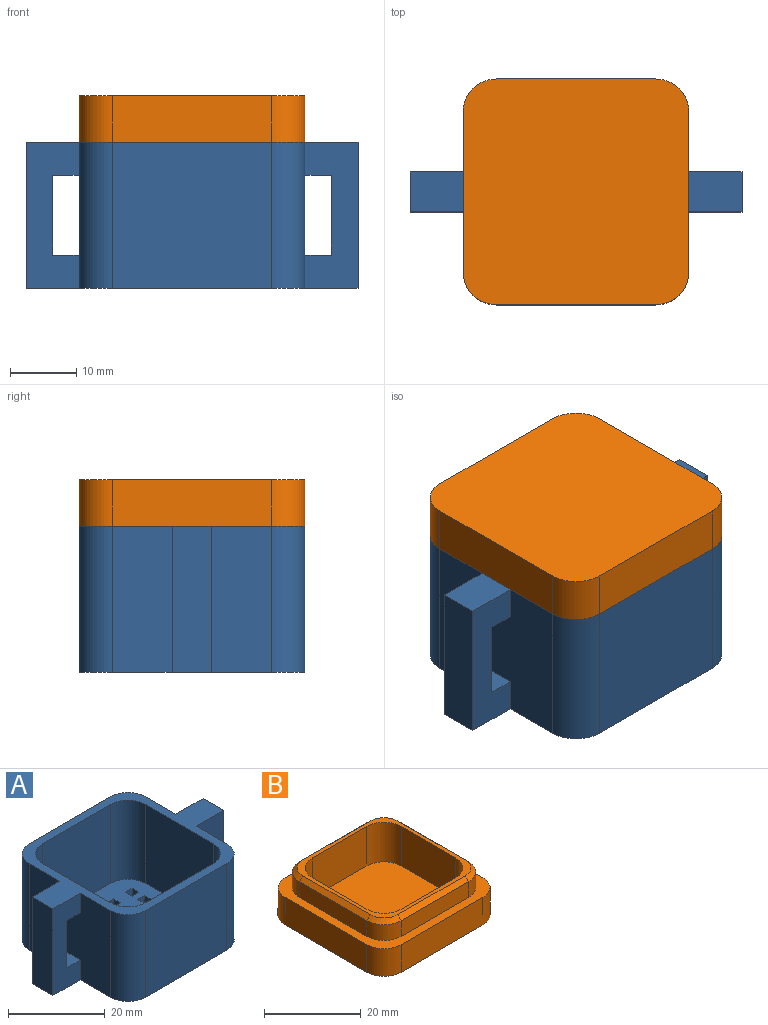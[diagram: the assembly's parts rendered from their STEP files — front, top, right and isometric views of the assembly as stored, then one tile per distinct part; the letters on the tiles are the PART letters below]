
ASSEMBLY  parts=2 mates=1
PART A: 77 faces, bbox 50x34x22 mm
  f0: plane 24x22mm, normal (-1,0,0), area 468mm2, adj f2,f10,f57,f58,f71,f72,f73,f76
  f1: plane 30x30mm, normal (0,0,1), area 738mm2, adj f5,f6,f7,f8,f11,f12,f13,f14
  f2: plane 50x34mm, normal (0,0,-1), area 1124.2mm2, adj f0,f3,f4,f9,f11,f12,f13,f14
  f3: plane 24x22mm, normal (0,1,0), area 528mm2, adj f2,f10,f57,f60
  f4: plane 24x22mm, normal (0,-1,0), area 528mm2, adj f2,f10,f58,f59
  f5: plane 20x20mm, normal (1,0,0), area 400mm2, adj f1,f10,f61,f64
  f6: plane 20x20mm, normal (0,-1,0), area 400mm2, adj f1,f10,f61,f62
  f7: plane 20x20mm, normal (-1,0,0), area 400mm2, adj f1,f10,f62,f63
  f8: plane 20x20mm, normal (0,1,0), area 400mm2, adj f1,f10,f63,f64
  f9: plane 24x22mm, normal (1,0,0), area 468mm2, adj f2,f10,f59,f60,f65,f66,f67,f70
  f10: plane 50x34mm, normal (0,0,1), area 352mm2, adj f0,f3,f4,f5,f6,f7,f8,f9
  f11: plane 2x2mm, normal (1,0,0), area 4mm2, adj f1,f2,f12,f14
  f12: plane 2x2mm, normal (0,-1,0), area 4mm2, adj f1,f2,f11,f13
  f13: plane 2x2mm, normal (-1,0,0), area 4mm2, adj f1,f2,f12,f14
  f14: plane 2x2mm, normal (0,1,0), area 4mm2, adj f1,f2,f11,f13
  f15: plane 2x2mm, normal (-1,0,0), area 4mm2, adj f1,f2,f16,f18
  f16: plane 2x2mm, normal (0,1,0), area 4mm2, adj f1,f2,f15,f17
  f17: plane 2x2mm, normal (1,0,0), area 4mm2, adj f1,f2,f16,f18
  f18: plane 2x2mm, normal (0,-1,0), area 4mm2, adj f1,f2,f15,f17
  f19: plane 2x2mm, normal (-1,0,0), area 4mm2, adj f1,f2,f20,f22
  f20: plane 2x2mm, normal (0,1,0), area 4mm2, adj f1,f2,f19,f21
  f21: plane 2x2mm, normal (1,0,0), area 4mm2, adj f1,f2,f20,f22
  f22: plane 2x2mm, normal (0,-1,0), area 4mm2, adj f1,f2,f19,f21
  f23: plane 2x2mm, normal (-1,0,0), area 4mm2, adj f1,f2,f24,f26
  f24: plane 2x2mm, normal (0,1,0), area 4mm2, adj f1,f2,f23,f25
  f25: plane 2x2mm, normal (1,0,0), area 4mm2, adj f1,f2,f24,f26
  f26: plane 2x2mm, normal (0,-1,0), area 4mm2, adj f1,f2,f23,f25
  f27: plane 2x2mm, normal (-1,0,0), area 4mm2, adj f1,f2,f28,f30
  f28: plane 2x2mm, normal (0,1,0), area 4mm2, adj f1,f2,f27,f29
  f29: plane 2x2mm, normal (1,0,0), area 4mm2, adj f1,f2,f28,f30
  f30: plane 2x2mm, normal (0,-1,0), area 4mm2, adj f1,f2,f27,f29
  f31: plane 2x2mm, normal (-1,0,0), area 4mm2, adj f1,f2,f32,f34
  f32: plane 2x2mm, normal (0,1,0), area 4mm2, adj f1,f2,f31,f33
  f33: plane 2x2mm, normal (1,0,0), area 4mm2, adj f1,f2,f32,f34
  f34: plane 2x2mm, normal (0,-1,0), area 4mm2, adj f1,f2,f31,f33
  f35: plane 2x2mm, normal (-1,0,0), area 4mm2, adj f1,f2,f36,f38
  f36: plane 2x2mm, normal (0,1,0), area 4mm2, adj f1,f2,f35,f37
  f37: plane 2x2mm, normal (1,0,0), area 4mm2, adj f1,f2,f36,f38
  f38: plane 2x2mm, normal (0,-1,0), area 4mm2, adj f1,f2,f35,f37
  f39: plane 2x2mm, normal (-1,0,0), area 4mm2, adj f1,f2,f40,f42
  f40: plane 2x2mm, normal (0,1,0), area 4mm2, adj f1,f2,f39,f41
  f41: plane 2x2mm, normal (1,0,0), area 4mm2, adj f1,f2,f40,f42
  f42: plane 2x2mm, normal (0,-1,0), area 4mm2, adj f1,f2,f39,f41
  f43: plane 2x2mm, normal (-1,0,0), area 4mm2, adj f1,f2,f44,f46
  f44: plane 2x2mm, normal (0,1,0), area 4mm2, adj f1,f2,f43,f45
  f45: plane 2x2mm, normal (1,0,0), area 4mm2, adj f1,f2,f44,f46
  f46: plane 2x2mm, normal (0,-1,0), area 4mm2, adj f1,f2,f43,f45
  f47: plane 2x2mm, normal (-1,0,0), area 4mm2, adj f1,f2,f48,f50
  f48: plane 2x2mm, normal (0,1,0), area 4mm2, adj f1,f2,f47,f49
  f49: plane 2x2mm, normal (1,0,0), area 4mm2, adj f1,f2,f48,f50
  f50: plane 2x2mm, normal (0,-1,0), area 4mm2, adj f1,f2,f47,f49
  f51: cylinder r=3.25mm len=6.5mm, axis (0,0,-1), area 81.7mm2, adj f2,f54
  f52: cylinder r=3.25mm len=6.5mm, axis (0,0,-1), area 81.7mm2, adj f2,f56
  f53: cylinder r=4mm len=8mm, axis (0,0,-1), area 50.3mm2, adj f1,f54
  f54: plane 8x8mm, normal (0,0,1), area 17.1mm2, adj f51,f53
  f55: cylinder r=4mm len=8mm, axis (0,0,-1), area 50.3mm2, adj f1,f56
  f56: plane 8x8mm, normal (0,0,1), area 17.1mm2, adj f52,f55
  f57: cylinder r=5mm len=22mm, axis (0,0,1), area 172.8mm2, adj f0,f2,f3,f10
  f58: cylinder r=5mm len=22mm, axis (0,0,-1), area 172.8mm2, adj f0,f2,f4,f10
  f59: cylinder r=5mm len=22mm, axis (0,0,1), area 172.8mm2, adj f2,f4,f9,f10
  f60: cylinder r=5mm len=22mm, axis (0,0,-1), area 172.8mm2, adj f2,f3,f9,f10
  f61: cylinder r=5mm len=20mm, axis (0,0,-1), area 157.1mm2, adj f1,f5,f6,f10
  f62: cylinder r=5mm len=20mm, axis (0,0,1), area 157.1mm2, adj f1,f6,f7,f10
  f63: cylinder r=5mm len=20mm, axis (0,0,-1), area 157.1mm2, adj f1,f7,f8,f10
  f64: cylinder r=5mm len=20mm, axis (0,0,1), area 157.1mm2, adj f1,f5,f8,f10
  f65: plane 22x8mm, normal (0,1,0), area 128mm2, adj f2,f9,f10,f66,f68,f69,f70
  f66: plane 6x4mm, normal (0,0,1), area 24mm2, adj f9,f65,f67,f69
  f67: plane 22x8mm, normal (0,-1,0), area 128mm2, adj f2,f9,f10,f66,f68,f69,f70
  f68: plane 22x6mm, normal (1,0,0), area 132mm2, adj f2,f10,f65,f67
  f69: plane 12x6mm, normal (-1,0,0), area 72mm2, adj f65,f66,f67,f70
  f70: plane 6x4mm, normal (0,0,-1), area 24mm2, adj f9,f65,f67,f69
  f71: plane 22x8mm, normal (0,1,0), area 128mm2, adj f0,f2,f10,f73,f74,f75,f76
  f72: plane 22x8mm, normal (0,-1,0), area 128mm2, adj f0,f2,f10,f73,f74,f75,f76
  f73: plane 6x4mm, normal (0,0,1), area 24mm2, adj f0,f71,f72,f75
  f74: plane 22x6mm, normal (-1,0,0), area 132mm2, adj f2,f10,f71,f72
  f75: plane 12x6mm, normal (1,0,0), area 72mm2, adj f71,f72,f73,f76
  f76: plane 6x4mm, normal (0,0,-1), area 24mm2, adj f0,f71,f72,f75
PART B: 36 faces, bbox 34x34x12 mm
  f0: plane 24x7mm, normal (0,1,0), area 168mm2, adj f4,f5,f6,f9
  f1: plane 24x7mm, normal (-1,0,0), area 168mm2, adj f4,f5,f6,f7
  f2: plane 24x7mm, normal (0,-1,0), area 168mm2, adj f4,f5,f7,f8
  f3: plane 24x7mm, normal (1,0,0), area 168mm2, adj f4,f5,f8,f9
  f4: plane 34x34mm, normal (0,0,-1), area 1134.5mm2, adj f0,f1,f2,f3,f6,f7,f8,f9
  f5: plane 34x34mm, normal (0,0,1), area 268mm2, adj f0,f1,f2,f3,f6,f7,f8,f9
  f6: cylinder r=5mm len=7mm, axis (0,0,1), area 55mm2, adj f0,f1,f4,f5
  f7: cylinder r=5mm len=7mm, axis (0,0,-1), area 55mm2, adj f1,f2,f4,f5
  f8: cylinder r=5mm len=7mm, axis (0,0,1), area 55mm2, adj f2,f3,f4,f5
  f9: cylinder r=5mm len=7mm, axis (0,0,-1), area 55mm2, adj f0,f3,f4,f5
  f10: plane 19.8x4mm, normal (-1,0,0), area 79.2mm2, adj f5,f20,f23,f35
  f11: plane 19.8x4mm, normal (0,-1,0), area 79.2mm2, adj f5,f20,f21,f32
  f12: plane 19.8x4mm, normal (1,0,0), area 79.2mm2, adj f5,f21,f22,f28
  f13: plane 19.8x4mm, normal (0,1,0), area 79.2mm2, adj f5,f22,f23,f31
  f14: plane 27.8x27.8mm, normal (0,0,1), area 104.6mm2, adj f16,f17,f18,f19,f24,f25,f26,f27
  f15: plane 26x26mm, normal (0,0,1), area 654.5mm2, adj f16,f17,f18,f19,f24,f25,f26,f27
  f16: plane 16x10mm, normal (-1,0,0), area 160mm2, adj f14,f15,f26,f27
  f17: plane 16x10mm, normal (0,-1,0), area 160mm2, adj f14,f15,f25,f26
  f18: plane 16x10mm, normal (1,0,0), area 160mm2, adj f14,f15,f24,f25
  f19: plane 16x10mm, normal (0,1,0), area 160mm2, adj f14,f15,f24,f27
  f20: cylinder r=5mm len=5mm, axis (0,0,-1), area 31.4mm2, adj f5,f10,f11,f34
  f21: cylinder r=5mm len=5mm, axis (0,0,1), area 31.4mm2, adj f5,f11,f12,f30
  f22: cylinder r=5mm len=5mm, axis (0,0,-1), area 31.4mm2, adj f5,f12,f13,f29
  f23: cylinder r=5mm len=5mm, axis (0,0,1), area 31.4mm2, adj f5,f10,f13,f33
  f24: cylinder r=5mm len=10mm, axis (0,0,1), area 78.5mm2, adj f14,f15,f18,f19
  f25: cylinder r=5mm len=10mm, axis (0,0,-1), area 78.5mm2, adj f14,f15,f17,f18
  f26: cylinder r=5mm len=10mm, axis (0,0,1), area 78.5mm2, adj f14,f15,f16,f17
  f27: cylinder r=5mm len=10mm, axis (0,0,-1), area 78.5mm2, adj f14,f15,f16,f19
  f28: plane 19.8x1mm, normal (0.71,0,0.71), area 28mm2, adj f12,f14,f29,f30
  f29: cone r=4mm half-angle=45deg, axis (0,0,-1), area 10mm2, adj f14,f22,f28,f31
  f30: cone r=4mm half-angle=45deg, axis (0,0,-1), area 10mm2, adj f14,f21,f28,f32
  f31: plane 19.8x1mm, normal (0,0.71,0.71), area 28mm2, adj f13,f14,f29,f33
  f32: plane 19.8x1mm, normal (0,-0.71,0.71), area 28mm2, adj f11,f14,f30,f34
  f33: cone r=4mm half-angle=45deg, axis (0,0,-1), area 10mm2, adj f14,f23,f31,f35
  f34: cone r=4mm half-angle=45deg, axis (0,0,-1), area 10mm2, adj f14,f20,f32,f35
  f35: plane 19.8x1mm, normal (-0.71,0,0.71), area 28mm2, adj f10,f14,f33,f34
PLACE A t=(52.86,-28.63,-36.08)mm
PLACE B rot(axis=(0,1,0),180deg) t=(-14.07,-24.08,-9.08)mm
MATE fastened A.f10 <-> B.f5  axis (0,0,1) through (52.86,-45.63,-16.08)mm
